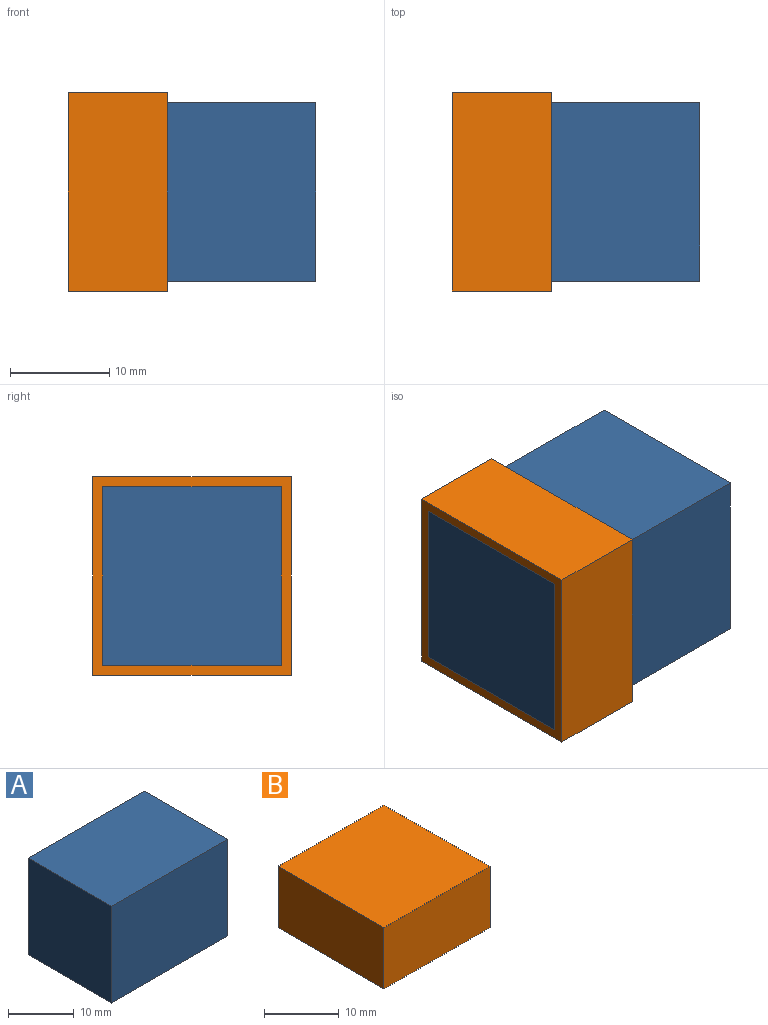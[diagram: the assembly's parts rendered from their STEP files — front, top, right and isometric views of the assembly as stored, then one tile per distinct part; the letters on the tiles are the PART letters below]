
ASSEMBLY  parts=2 mates=1
PART A: 6 faces, bbox 25x18x18 mm
  f0: plane 25x18mm, normal (0,0,1), area 450mm2, adj f1,f3,f4,f5
  f1: plane 25x18mm, normal (0,-1,0), area 450mm2, adj f0,f2,f4,f5
  f2: plane 25x18mm, normal (0,0,-1), area 450mm2, adj f1,f3,f4,f5
  f3: plane 25x18mm, normal (0,1,0), area 450mm2, adj f0,f2,f4,f5
  f4: plane 18x18mm, normal (1,0,0), area 324mm2, adj f0,f1,f2,f3
  f5: plane 18x18mm, normal (-1,0,0), area 324mm2, adj f0,f1,f2,f3
PART B: 6 faces, bbox 20x20x10 mm
  f0: plane 20x10mm, normal (0,1,0), area 200mm2, adj f1,f3,f4,f5
  f1: plane 20x10mm, normal (-1,0,0), area 200mm2, adj f0,f2,f4,f5
  f2: plane 20x10mm, normal (0,-1,0), area 200mm2, adj f1,f3,f4,f5
  f3: plane 20x10mm, normal (1,0,0), area 200mm2, adj f0,f2,f4,f5
  f4: plane 20x20mm, normal (0,0,1), area 400mm2, adj f0,f1,f2,f3
  f5: plane 20x20mm, normal (0,0,-1), area 400mm2, adj f0,f1,f2,f3
PLACE A t=(-9.23,-7.75,-56.97)mm
PLACE B rot(axis=(0,-1,0),90deg) t=(16.26,-5.56,28.01)mm
MATE parallel B.f4 <-> A.f5  axis (-1,0,0) through (6.26,-1.39,33.5)mm
